# Revit family: CNA40x60
name_source: partatom
category: Detail Items
revit_build: Autodesk Revit 2014 (Build: 20130308_1515(x64)
units: mm (PartAtom-declared; Revit-internal decimal feet)

## types (2) — shared parameters
Density = 0.01 kg
Description = Nails
EPD = https://www.strongtie.eu
ETA / DoP = https://www.strongtie.eu
Manufacturer = Simpson Strong-Tie
Model = CNA4.0x60
Model Disclaimer = Contact Simpson Strong-Tie Company  for more information
Model ID = 0292902917112128702876334243493600675948
Name = CNA4.0x60
ObjectType = CNA4.0x60
Product Material = ElectroGalvanised
Product Type = Nails
Reference = CNA4.0x60
Technical datasheet = https://www.strongtie.eu
URL = www.strongtie.eu
UniClass Number = Pr_20_29_76_98
UniClass Title = Wood screws

## per-type parameters (varying)
| type | _visiblefront | _visibletop |
| SST_CNA4.0x60_Front | Yes | No |
| SST_CNA4.0x60_Top | No | Yes |

## geometry (parser evidence)
native form markers: Sweep x2
no freeform markers — native parametric forms only
